# Revit family: Elevator_COM_NationwideLifts_Freedom-LULA
name_source: partatom
category: Generic Models
units: mm (PartAtom-declared; Revit-internal decimal feet)

## family parameters
Always vertical = No
Can host rebar = No
Classification Number = 23.50.05.11.14
Cut with Voids When Loaded = No
Maintain Annotation Orientation = No
Part Type = Normal
Room Calculation Point = No
Round Connector Dimension = Use Diameter
Shared = No
Work Plane-Based = Yes

## types (6) — shared parameters
Assembly Code = D1010100
Cab Style 2 Sliding Panel = Yes
Cab Style Accordian Gate = No
Capacity = 1000 lbs
Center of Door A = 3' - 5"
Center of Door B = 0' - 0"
Default Elevation = 0' - 0"
Description = Nationwide Lifts Commercial Hydraulic Elevator - Freedom Commercial LULA as Specified
Keynote = 14 20 00
Lift Height = 0' - 0"
Lift Travel Speed = 30 fpm and 25 ft of Travel
Manufacturer = Nationwide Lifts, Inc.
Manufacturer Website = http://www.elevators.com
Opening Width = 5' - 9"
Product Data = http://www.arcat.com
Revision = R1_2016-05
Sales Information = http://www.elevators.com
Space Between Cab and Hoistway = 0' - 2"
Specification = http://www.arcat.com
Standards Conformance = ADA  ;  Cannot fit a gurney
URL = http://www.elevators.com
zero-valued in all types: Expected Lifespan (Years), Maintenance Schedule (Months), Warranty Duration (Years)

## per-type parameters (varying)
| type | Cab Design | Center of Rail | Model | Opening Depth | Unit Depth | Unit Width |
| Type 2 48 x 54 | Cab_Type2 | 3' - 4" | Freedom Commercial LULA Type 2 | 6' - 8" | 4' - 6" | 4' - 0" |
| Type 2 42 x 60 | Cab_Type2 | 3' - 7" | Freedom Commercial LULA Type 2 | 7' - 2" | 5' - 0" | 3' - 6" |
| Type 1R 48 x 54 | Cab_Type1R | 3' - 4" | Freedom Commercial LULA Type 1R | 6' - 1" | 4' - 6" | 4' - 0" |
| Type 1R 42 x 60 | Cab_Type1R | 3' - 7" | Freedom Commercial LULA Type 1R | 6' - 7" | 5' - 0" | 3' - 6" |
| Type 1L 48 x 54 | Cab_Type1L | 3' - 4" | Freedom Commercial LULA Type 1L | 6' - 1" | 4' - 6" | 4' - 0" |
| Type 1L 42 x 60 | Cab_Type1L | 3' - 7" | Freedom Commercial LULA Type 1L | 6' - 7" | 5' - 0" | 3' - 6" |

## geometry (parser evidence)
native form markers: Sweep x15
no freeform markers — native parametric forms only
